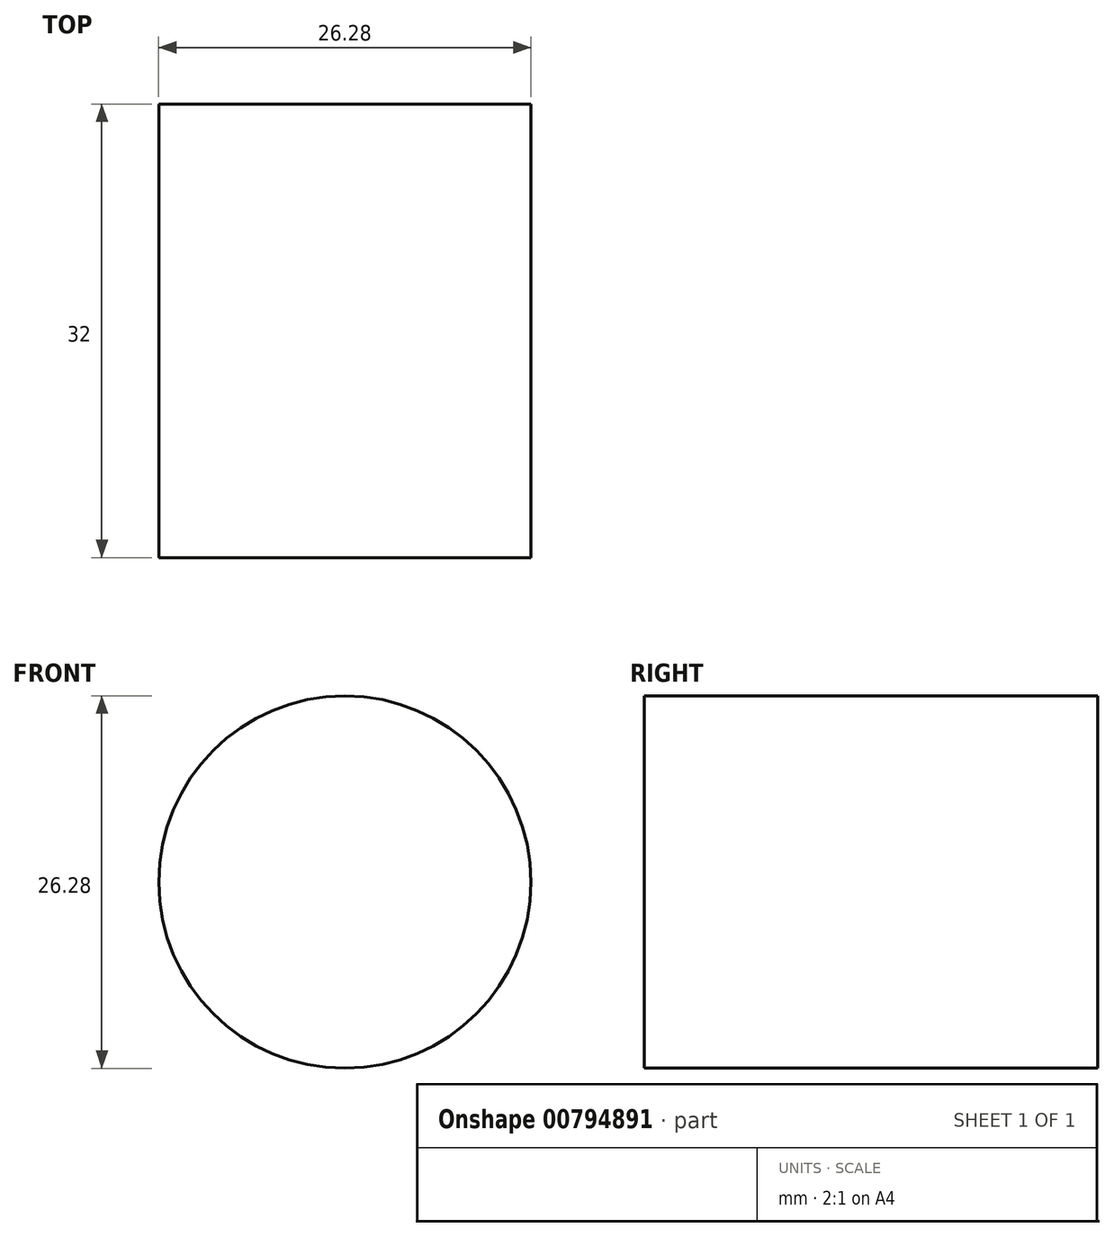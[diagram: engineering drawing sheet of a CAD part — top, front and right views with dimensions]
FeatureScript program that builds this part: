
annotation { "Feature Type Name" : "Feature", "Feature Type Description" : "" }
export const myFeature = defineFeature(function(context is Context, id is Id, definition is map)
    precondition{}
    {
        {
            var Q0;
            Q0=qCreatedBy(makeId("Front.planeOp"),FACE);
            var sketch = newSketch(context, id + "F0", { "sketchPlane" : qUnion([Q0])});
            skCircle(sketch, "E0", {"center": v(0, 0) * mm, "radius": 13.14 * mm});
            skSolve(sketch);
        }
        {
            var Q0;
            Q0=makeQuery(id+"F0.imprint","IMPRINT",FACE,{"disambiguationData":[TD([[makeQuery(id+"F0.imprint","IMPRINT",EDGE,{"derivedFrom":sQuery(id+"F0.wireOp",EDGE,"E0")}),1.0]])]});
            extrude(context, id + "F1", {"entities" : qUnion([Q0]), "depth" : 32 * mm, "offsetDistance" : 25.4 * mm});
        }
    });
